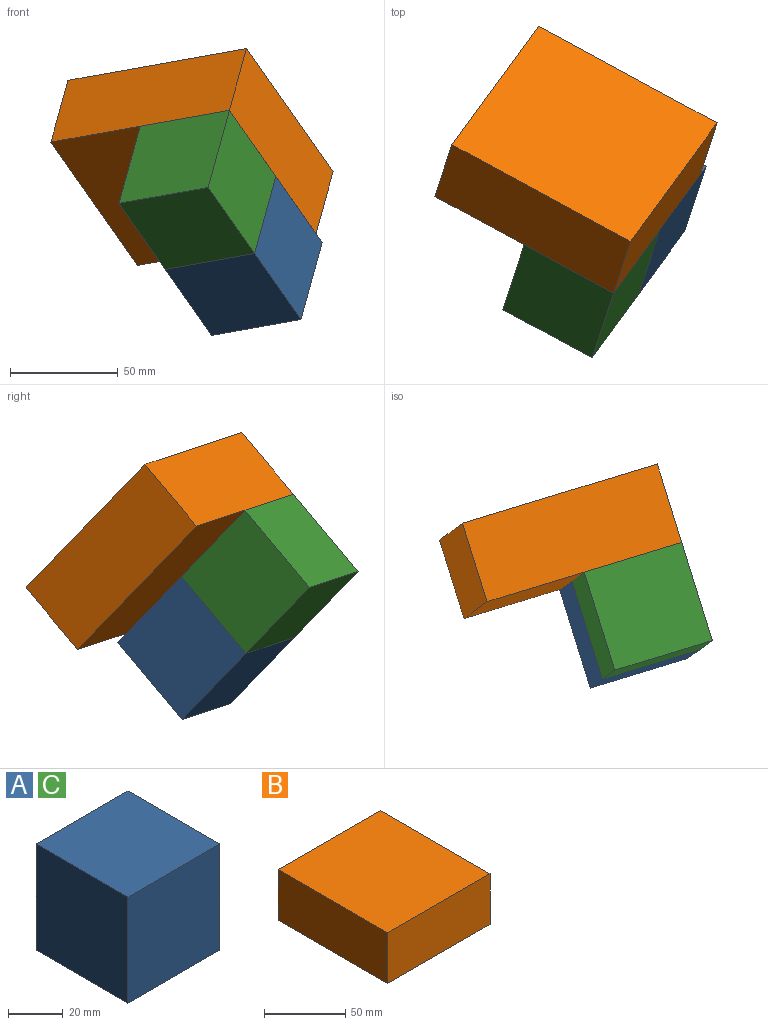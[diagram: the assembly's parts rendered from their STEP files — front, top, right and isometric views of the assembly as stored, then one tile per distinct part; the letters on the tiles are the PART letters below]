
ASSEMBLY  parts=3 mates=4
PART A: 6 faces, bbox 47.6x47.6x47.6 mm
  f0: plane 47.63x47.63mm, normal (0,1,0), area 2268.1mm2, adj f1,f3,f4,f5
  f1: plane 47.63x47.63mm, normal (-1,0,0), area 2268.1mm2, adj f0,f2,f4,f5
  f2: plane 47.63x47.63mm, normal (0,-1,0), area 2268.1mm2, adj f1,f3,f4,f5
  f3: plane 47.63x47.63mm, normal (1,0,0), area 2268.1mm2, adj f0,f2,f4,f5
  f4: plane 47.63x47.63mm, normal (0,0,1), area 2268.1mm2, adj f0,f1,f2,f3
  f5: plane 47.63x47.63mm, normal (0,0,-1), area 2268.1mm2, adj f0,f1,f2,f3
PART B: 6 faces, bbox 88.9x95.3x38.1 mm
  f0: plane 88.9x38.1mm, normal (0,1,0), area 3387.1mm2, adj f1,f3,f4,f5
  f1: plane 95.25x38.1mm, normal (-1,0,0), area 3629mm2, adj f0,f2,f4,f5
  f2: plane 88.9x38.1mm, normal (0,-1,0), area 3387.1mm2, adj f1,f3,f4,f5
  f3: plane 95.25x38.1mm, normal (1,0,0), area 3629mm2, adj f0,f2,f4,f5
  f4: plane 95.25x88.9mm, normal (0,0,1), area 8467.7mm2, adj f0,f1,f2,f3
  f5: plane 95.25x88.9mm, normal (0,0,-1), area 8467.7mm2, adj f0,f1,f2,f3
PART C: same geometry as A
PLACE A rot(axis=(0.63,-0.43,-0.65),172.2deg) t=(-109.2,-19,-134.88)mm
PLACE B rot(axis=(-0.29,-0.27,-0.92),125.9deg) t=(-145.63,31.64,-88.36)mm
PLACE C rot(axis=(-0.29,-0.27,-0.92),125.9deg) t=(-122.33,-47.16,-92.36)mm
MATE planar B.f3 <-> C.f3  axis (-0.45,-0.62,0.64) through (-152.02,28.28,-58.4)mm
MATE fastened C.f1 <-> A.f0  axis (0.45,0.62,-0.64) through (-118.73,19.65,-117.48)mm
MATE planar A.f1 <-> B.f5  axis (0.21,0.63,0.75) through (-103.06,49.35,-114.9)mm
MATE planar A.f5 <-> B.f0  axis (0.87,-0.47,0.15) through (-87.32,23.17,-129.09)mm
